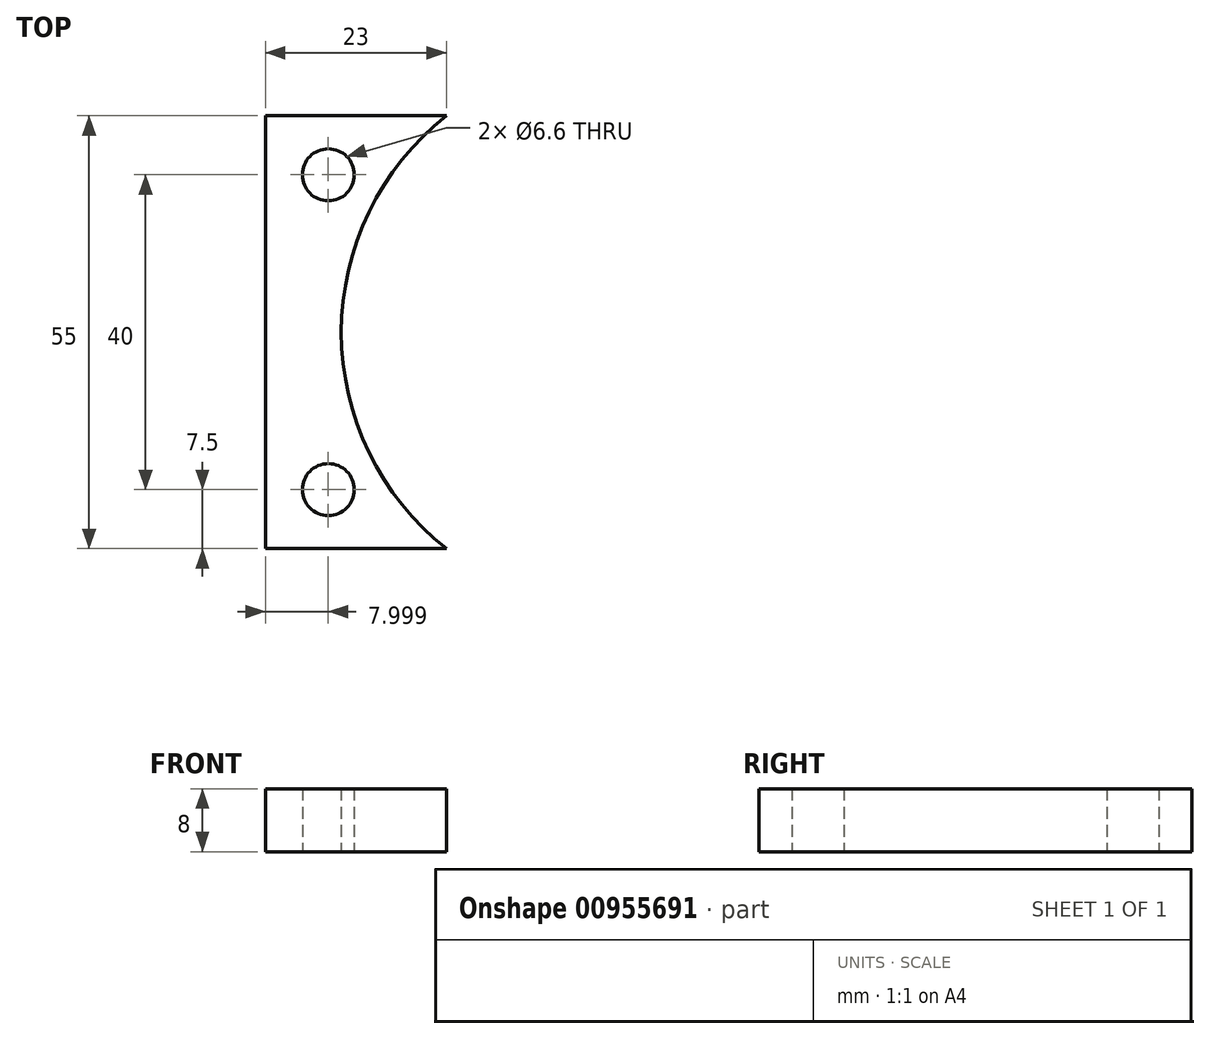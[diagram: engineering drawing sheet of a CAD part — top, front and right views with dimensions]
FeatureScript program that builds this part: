
annotation { "Feature Type Name" : "Feature", "Feature Type Description" : "" }
export const myFeature = defineFeature(function(context is Context, id is Id, definition is map)
    precondition{}
    {
        {
            var Q0;
            Q0=qCreatedBy(makeId("Top.planeOp"),FACE);
            var sketch = newSketch(context, id + "F0", { "sketchPlane" : qUnion([Q0])});
            skArc(sketch, "E0", {"start": v(-24.5, 25) * mm, "mid": v(-35, 0) * mm, "end": v(-24.5, -25) * mm});
            skArc(sketch, "E1", {"start": v(-21.65, 27.5) * mm, "mid": v(-35, 0) * mm, "end": v(-21.65, -27.5) * mm});
            skPoint(sketch, "E2", {"position": v(-21.65, 27.5) * mm});
            skPoint(sketch, "E3", {"position": v(-21.65, -27.5) * mm});
            skLineSegment(sketch, "E4", {"start": v(-21.65, 27.5) * mm, "end": v(-44.65, 27.5) * mm});
            skLineSegment(sketch, "E5", {"start": v(-21.65, -27.5) * mm, "end": v(-44.65, -27.5) * mm});
            skLineSegment(sketch, "E6", {"start": v(-44.65, -27.5) * mm, "end": v(-44.65, 27.5) * mm});
            skCircle(sketch, "E7", {"center": v(0, 0) * mm, "radius": 35 * mm});
            skSolve(sketch);
        }
        {
            var Q0;
            {var subQ0=sQuery(id+"F0.wireOp",EDGE,"E6");Q0=makeQuery(id+"F0.imprint","IMPRINT",FACE,{"disambiguationData":[TD([[makeQuery(id+"F0.imprint","IMPRINT",EDGE,{"derivedFrom":subQ0}),-1.0]])]});}
            extrude(context, id + "F1", {"entities" : qUnion([Q0]), "depth" : 8 * mm, "offsetDistance" : 25 * mm});
        }
        {
            var Q0;
            Q0=makeQuery(id+"F1.opExtrude","CAP_FACE",FACE,{"disambiguationData":[OSD([sQuery(id+"F0.wireOp",EDGE,"E1"),sQuery(id+"F0.wireOp",EDGE,"E4"),sQuery(id+"F0.wireOp",EDGE,"E5"),sQuery(id+"F0.wireOp",EDGE,"E6")])],"isStart":true});
            var sketch = newSketch(context, id + "F2", { "sketchPlane" : qUnion([Q0])});
            skPoint(sketch, "E8", {"position": v(-36.65, 20) * mm});
            skPoint(sketch, "E9", {"position": v(-36.65, -20) * mm});
            skSolve(sketch);
        }
        {
            var Q0;
            Q0=sQuery(id+"F2.wireOp",VERTEX,"E8");
            var Q1;
            Q1=sQuery(id+"F2.wireOp",VERTEX,"E9");
            var Q2;
            Q2=makeQuery(id+"F1.opExtrude","SWEPT_BODY",BODY,{"disambiguationData":[OSD([sQuery(id+"F0.wireOp",EDGE,"E1"),sQuery(id+"F0.wireOp",EDGE,"E4"),sQuery(id+"F0.wireOp",EDGE,"E5"),sQuery(id+"F0.wireOp",EDGE,"E6")])]});
            hole(context, id + "F3", {"style" : HoleStyle.SIMPLE, "endStyle" : HoleEndStyle.THROUGH, "holeDiameter" : 6.6 * mm, "majorDiameter" : 5 * mm, "isTappedThrough" : true, "tappedDepth" : 7.9 * mm, "tapClearance" : 3, "startFromSketch" : true, "locations" : qUnion([Q0, Q1]), "scope" : qUnion([Q2])});
        }
    });
